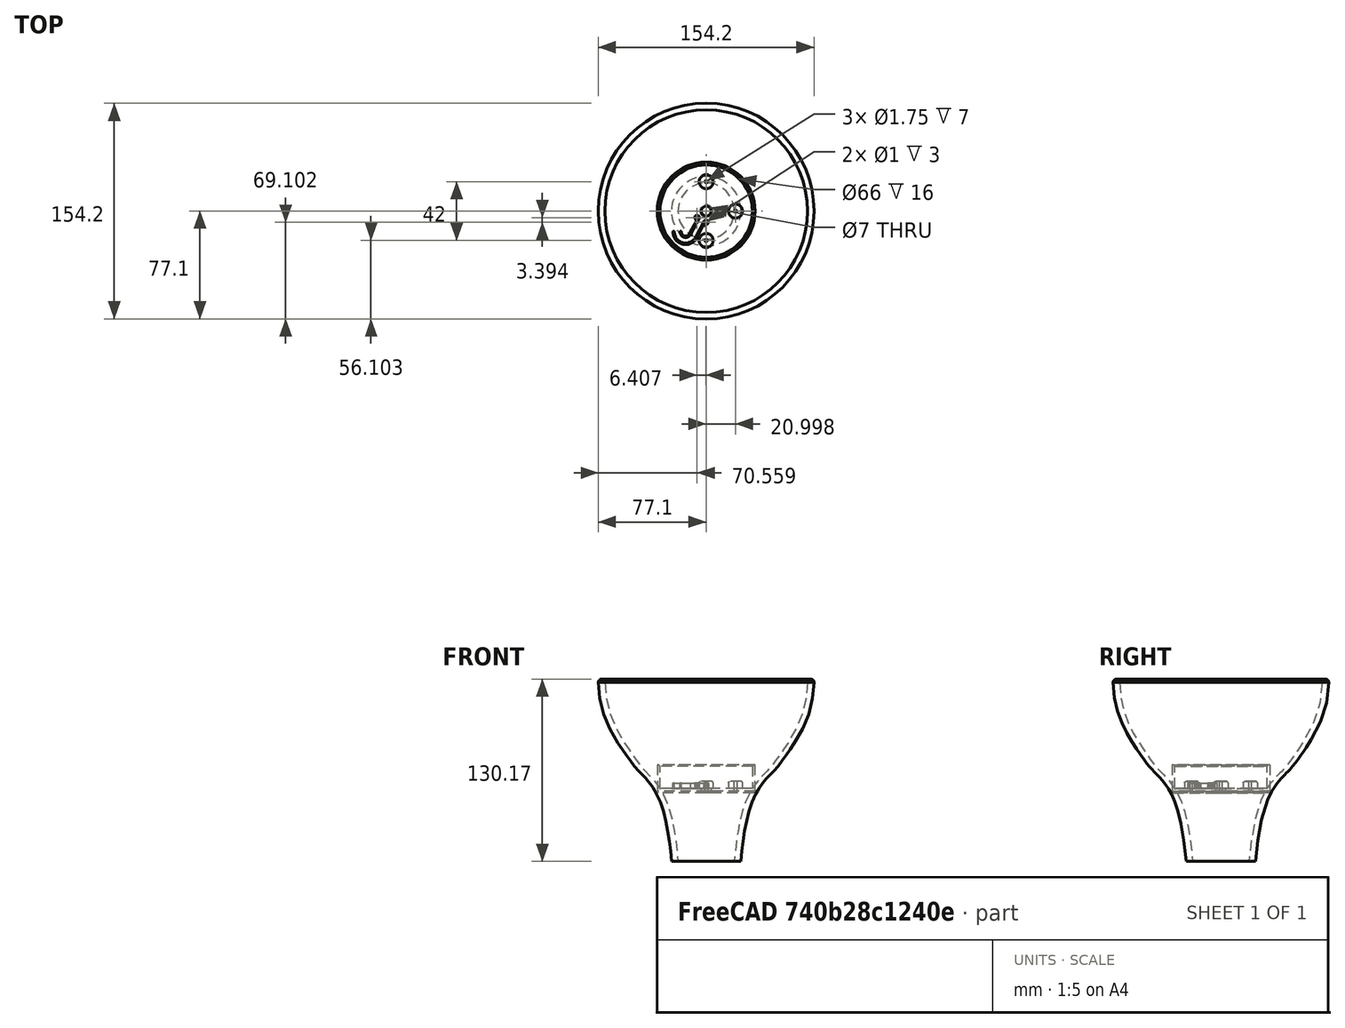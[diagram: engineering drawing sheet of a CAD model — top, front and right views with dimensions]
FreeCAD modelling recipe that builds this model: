
FCSTD DOCUMENT  (FreeCAD 0.21R33771 (Git))
Label: lampshade pre-merge
License: All rights reserved
LicenseURL: http://en.wikipedia.org/wiki/All_rights_reserved
objects: Sketcher::SketchObject×9, PartDesign::Pocket×4, PartDesign::Fillet×4, PartDesign::Pad×3, Part::Feature×2, PartDesign::Body×2, PartDesign::Chamfer×1, Mesh::Feature×1, Part::Refine×1, PartDesign::Revolution×1, App::Part×1
note: 40 computed .brp shape members not serialized (recipe doc carries the construction recipe); baked Part::Feature solids carry a one-line shape summary decoded from their .brp

FEATURE [Sketcher::SketchObject] Sketch001
  FullyConstrained = true
  MapMode = 5
  Support = -> [XY_Plane]
  sketch-geometry (1):
    g0: Circle CenterX=0 CenterY=0 CenterZ=0 NormalX=0 NormalY=0 NormalZ=1 AngleXU=0 Radius=35
  constraints (2):
    c: Coincident(g0,g-1)
    c: Diameter(g0) = 70
FEATURE [PartDesign::Pad] Pad
  Direction = (0,0,1)
  Length = 20
  Length2 = 10
  Profile = -> Sketch001
  ReferenceAxis = -> Sketch001 [N_Axis]
  Type = 0
FEATURE [Sketcher::SketchObject] Sketch
  FullyConstrained = true
  MapMode = 5
  Placement = pos=(0,0,20) rot=(0,0,1;0rad)
  Support = -> [Pad]
  sketch-geometry (1):
    g0: Circle CenterX=0 CenterY=0 CenterZ=0 NormalX=0 NormalY=0 NormalZ=1 AngleXU=0 Radius=33
  constraints (2):
    c: Coincident(g0,g-1)
    c: Diameter(g0) = 66
FEATURE [PartDesign::Pocket] Pocket
  BaseFeature = -> Pad
  Direction = (0,0,-1)
  Length = 17
  Length2 = 5
  Profile = -> Sketch
  ReferenceAxis = -> Sketch [N_Axis]
  Type = 0
FEATURE [Sketcher::SketchObject] Sketch002
  FullyConstrained = false
  MapMode = 5
  Placement = pos=(0,0,3) rot=(0,0,1;0rad)
  Support = -> [Pocket]
  sketch-geometry (4):
    g0: Circle CenterX=-0.00194019 CenterY=0.00345167 CenterZ=0 NormalX=0 NormalY=0 NormalZ=1 AngleXU=0 Radius=21
    g1: Circle CenterX=0 CenterY=21.0035 CenterZ=0 NormalX=0 NormalY=0 NormalZ=1 AngleXU=0 Radius=5
    g2: Circle CenterX=20.9981 CenterY=0 CenterZ=0 NormalX=0 NormalY=0 NormalZ=1 AngleXU=0 Radius=5
    g3: Circle CenterX=0 CenterY=-20.9965 CenterZ=0 NormalX=0 NormalY=0 NormalZ=1 AngleXU=0 Radius=5
  constraints (10):
    c: Diameter(g0) = 42
    c: PointOnObject(g1,g0)
    c: PointOnObject(g2,g0)
    c: PointOnObject(g3,g0)
    c: PointOnObject(g3,g-2)
    c: PointOnObject(g2,g-1)
    c: PointOnObject(g1,g-2)
    c: Equal(g1,g2)
    c: Equal(g2,g3)
    c: Diameter(g1) = 10
FEATURE [PartDesign::Pad] Pad001
  BaseFeature = -> Pocket
  Direction = (0,0,1)
  Length = 5
  Length2 = 10
  Profile = -> Sketch002
  ReferenceAxis = -> Sketch002 [N_Axis]
  Type = 0
FEATURE [Sketcher::SketchObject] Sketch003
  ExternalGeometry = -> [Pad001]
  FullyConstrained = true
  MapMode = 5
  Placement = pos=(0,0,8) rot=(0,0,1;0rad)
  Support = -> [Pad001]
  sketch-geometry (3):
    g0: Circle CenterX=0 CenterY=21.0035 CenterZ=0 NormalX=0 NormalY=0 NormalZ=1 AngleXU=0 Radius=0.875
    g1: Circle CenterX=0 CenterY=-20.9965 CenterZ=0 NormalX=0 NormalY=0 NormalZ=1 AngleXU=0 Radius=0.875
    g2: Circle CenterX=20.9981 CenterY=0 CenterZ=0 NormalX=0 NormalY=0 NormalZ=1 AngleXU=0 Radius=0.875
  constraints (6):
    c: Coincident(g0,g-3)
    c: Coincident(g1,g-4)
    c: Coincident(g2,g-5)
    c: Equal(g0,g1)
    c: Equal(g1,g2)
    c: Diameter(g0) = 1.75
FEATURE [PartDesign::Pocket] Pocket001
  BaseFeature = -> Pad001
  Direction = (0,0,-1)
  Length = 7
  Length2 = 5
  Profile = -> Sketch003
  ReferenceAxis = -> Sketch003 [N_Axis]
  Type = 0
FEATURE [Sketcher::SketchObject] Sketch004
  FullyConstrained = true
  MapMode = 5
  Placement = pos=(0,0,3) rot=(0,0,1;0rad)
  Support = -> [Pocket001]
  sketch-geometry (1):
    g0: Circle CenterX=0 CenterY=0 CenterZ=0 NormalX=0 NormalY=0 NormalZ=1 AngleXU=0 Radius=3.5
  constraints (3):
    c: PointOnObject(g0,g-1)
    c: Diameter(g0) = 7
    c: PointOnObject(g0,g-2)
FEATURE [PartDesign::Pocket] Pocket002
  BaseFeature = -> Pocket001
  Direction = (0,0,-1)
  Length = 10
  Length2 = 5
  Profile = -> Sketch004
  ReferenceAxis = -> Sketch004 [N_Axis]
  Type = 0
FEATURE [PartDesign::Chamfer] Chamfer
  Angle = 45
  Base = -> Pocket002 [Edge2,Edge5,Edge4]
  BaseFeature = -> Pocket002
  ChamferType = 0
  FlipDirection = false
  Size = 1
  Size2 = 1
  SupportTransform = false
  UseAllEdges = false
FEATURE [Sketcher::SketchObject] Sketch005
  ExternalGeometry = -> [Chamfer]
  FullyConstrained = false
  MapMode = 5
  Placement = pos=(0,0,3) rot=(0,0,1;0rad)
  Support = -> [Chamfer]
  sketch-geometry (21):
    g0: LineSegment StartX=0 StartY=0 StartZ=0 EndX=-12.3375 EndY=-23.2904 EndZ=0
    g1: LineSegment StartX=-3.33785 StartY=-6.30109 StartZ=0 EndX=-5.10519 EndY=-5.36488 EndZ=0
    g2: LineSegment StartX=-3.33785 StartY=-6.30109 StartZ=0 EndX=-1.5705 EndY=-7.2373 EndZ=0
    g3: ArcOfCircle CenterX=-0.134531 CenterY=-7.99797 CenterZ=0 NormalX=0 NormalY=0 NormalZ=1 AngleXU=0 Radius=1.625 StartAngle=3.81788 EndAngle=8.93763
    g4: ArcOfCircle CenterX=-6.54116 CenterY=-4.60421 CenterZ=0 NormalX=0 NormalY=0 NormalZ=1 AngleXU=0 Radius=1.625 StartAngle=5.79576 EndAngle=10.9054
    g5: ArcOfCircle CenterX=-14.6925 CenterY=-14.9185 CenterZ=0 NormalX=0 NormalY=0 NormalZ=1 AngleXU=0 Radius=4 StartAngle=3.14159 EndAngle=5.83833
    g6: LineSegment StartX=-11.1578 StartY=-16.7909 StartZ=0 EndX=-9.3905 EndY=-17.7271 EndZ=0
    g7: LineSegment StartX=-9.3905 StartY=-17.7271 StartZ=0 EndX=-7.62315 EndY=-18.6633 EndZ=0
    g8: LineSegment StartX=-14.9937 StartY=-18.9071 StartZ=0 EndX=-14.9184 EndY=-17.91 EndZ=0
    g9: ArcOfCircle CenterX=-14.6925 CenterY=-14.9185 CenterZ=0 NormalX=0 NormalY=0 NormalZ=1 AngleXU=0 Radius=3 StartAngle=3.14159 EndAngle=5.79576
    g10: LineSegment StartX=-8.32768 StartY=-19.765 StartZ=0 EndX=-7.53208 EndY=-20.3708 EndZ=0
    g11: LineSegment StartX=-11.0819 StartY=-16.6398 StartZ=0 EndX=-5.10541 EndY=-5.36528 EndZ=0
    g12: LineSegment StartX=-7.62315 StartY=-18.6633 StartZ=0 EndX=-1.5705 EndY=-7.2373 EndZ=0
    g13: LineSegment StartX=-6.48386 StartY=-18.6087 StartZ=0 EndX=-1.40187 EndY=-9.01506 EndZ=0
    g14: LineSegment StartX=-12.0419 StartY=-16.3235 StartZ=0 EndX=-6.68757 EndY=-6.2226 EndZ=0
    g15: LineSegment StartX=-14.6925 StartY=-14.9185 StartZ=0 EndX=-23.6925 EndY=-14.9185 EndZ=0
    g16: ArcOfCircle CenterX=-23.1925 CenterY=-14.9185 CenterZ=0 NormalX=0 NormalY=0 NormalZ=1 AngleXU=0 Radius=0.5 StartAngle=0 EndAngle=3.14159
    g17: ArcOfCircle CenterX=-18.1925 CenterY=-14.9185 CenterZ=0 NormalX=0 NormalY=0 NormalZ=1 AngleXU=0 Radius=0.5 StartAngle=-9e-16 EndAngle=3.14159
    g18: GeomPoint X=-22.6925 Y=-14.9185 Z=0
    g19: ArcOfCircle CenterX=-14.6925 CenterY=-14.9185 CenterZ=0 NormalX=0 NormalY=0 NormalZ=1 AngleXU=0 Radius=9 StartAngle=3.14159 EndAngle=5.86071
    g20: ArcOfCircle CenterX=-14.6925 CenterY=-14.9185 CenterZ=0 NormalX=0 NormalY=0 NormalZ=1 AngleXU=0 Radius=8 StartAngle=3.14159 EndAngle=5.79604
  constraints (45):
    c: Coincident(g0,g-3)
    c: Coincident(g2,g1)
    c: PointOnObject(g1,g0)
    c: Perpendicular(g0,g1)
    c: Perpendicular(g0,g2)
    c: Equal(g1,g2)
    c: Distance(g1,g2) = 4
    c: PointOnObject(g1,g4)
    c: Perpendicular(g4,g1)
    c: Equal(g4,g3)
    c: Diameter(g3) = 3.25
    c: Diameter(g5) = 8
    c: PointOnObject(g6,g5)
    c: Coincident(g7,g6)
    c: Perpendicular(g5,g6)
    c: Equal(g6,g7)
    c: PointOnObject(g6,g0)
    c: Perpendicular(g0,g6)
    c: PointOnObject(g8,g5)
    c: Perpendicular(g5,g8)
    c: Distance(g8) = 1  'cable guide wall thickness'
    c: Coincident(g9,g5)
    c: PointOnObject(g8,g9)
    c: Equal(g8,g10)
    c: Tangent(g12,g3) = 1.5708
    c: Parallel(g14,g11)
    c: Parallel(g12,g13)
    c: Coincident(g15,g5)
    c: Horizontal(g15)
    c: PointOnObject(g16,g15)
    c: PointOnObject(g17,g15)
    c: PointOnObject(g18,g16)
    c: Coincident(g19,g13)
    c: Coincident(g20,g12) = -1.5708
    c: Perpendicular(g3,g2) = 1.5708
    c: Coincident(g3,g13)
    c: Coincident(g4,g14)
    c: Tangent(g4,g11) = -1.5708
    c: Tangent(g16,g19) = -1.5708
    c: Tangent(g16,g20) = 1.5708
    c: Tangent(g17,g9) = 1.5708
    c: Tangent(g5,g17) = -1.5708
    c: Tangent(g9,g14) = -1.5708
    c: PointOnObject(g9,g15)
    c: Coincident(g5,g11)
FEATURE [PartDesign::Pad] Pad002
  BaseFeature = -> Chamfer
  Direction = (0,0,1)
  Length = 3.75
  Length2 = 10
  Profile = -> Sketch005
  ReferenceAxis = -> Sketch005 [N_Axis]
  Type = 0
FEATURE [Sketcher::SketchObject] Sketch006
  ExternalGeometry = -> [Pad002]
  FullyConstrained = true
  MapMode = 5
  Placement = pos=(0,0,6.75) rot=(0,0,1;0rad)
  Support = -> [Pad002]
  sketch-geometry (2):
    g0: Circle CenterX=-6.54116 CenterY=-4.60421 CenterZ=0 NormalX=0 NormalY=0 NormalZ=1 AngleXU=0 Radius=0.5
    g1: Circle CenterX=-0.134531 CenterY=-7.99797 CenterZ=0 NormalX=0 NormalY=0 NormalZ=1 AngleXU=0 Radius=0.5
  constraints (4):
    c: Coincident(g0,g-3)
    c: Coincident(g1,g-4)
    c: Equal(g0,g1)
    c: Diameter(g0) = 1
FEATURE [PartDesign::Pocket] Pocket003
  BaseFeature = -> Pad002
  Direction = (0,0,-1)
  Length = 3
  Length2 = 5
  Profile = -> Sketch006
  ReferenceAxis = -> Sketch006 [N_Axis]
  Type = 0
FEATURE [PartDesign::Fillet] Fillet
  Base = -> Pocket003 [Edge15]
  BaseFeature = -> Pocket003
  Radius = 1
  SupportTransform = false
  UseAllEdges = false
FEATURE [PartDesign::Fillet] Fillet001
  Base = -> Fillet [Edge21]
  BaseFeature = -> Fillet
  Radius = 1
  SupportTransform = false
  UseAllEdges = false
FEATURE [PartDesign::Fillet] Fillet002
  Base = -> Fillet001 [Edge13]
  BaseFeature = -> Fillet001
  Radius = 1
  SupportTransform = false
  UseAllEdges = false
FEATURE [PartDesign::Fillet] Fillet003
  Base = -> Fillet002 [Edge49,Edge47,Edge51]
  BaseFeature = -> Fillet002
  Radius = 1
  SupportTransform = false
  UseAllEdges = false
FEATURE [Mesh::Feature] Head_v1
FEATURE [Part::Feature] Head_v002
  shape: large baked B-rep (101 MB .brp); summary skipped
FEATURE [Part::Refine] Head_v003
  Source = -> Head_v002
FEATURE [Part::Feature] Head_v003_cs
  shape: bbox 3e-07 x 154.9 x 129.2 mm, 0 faces, 0 solids (baked)
FEATURE [Sketcher::SketchObject] Sketch007
  FullyConstrained = false
  Placement = pos=(0,0,0) rot=(0,1,0;1.5708rad)
  sketch-geometry (18):
    g0: GeomPoint X=-127.837 Y=-77.1037 Z=0
    g1: BSplineCurve PolesCount=7 KnotsCount=5 Degree=3 IsPeriodic=0
    g2-g8: Circle x7 (B-spline internal-alignment scaffolding for g1; pole/knot coordinates omitted)
    g9-g13: GeomPoint x5 (B-spline internal-alignment scaffolding for g1; pole/knot coordinates omitted)
    g14: LineSegment StartX=-127.837 StartY=-77.1037 StartZ=0 EndX=-127.837 EndY=-72.4339 EndZ=0
    g15: BSplineCurve PolesCount=7 KnotsCount=5 Degree=3 IsPeriodic=0
    g16: LineSegment StartX=0 StartY=-24.806 StartZ=0 EndX=0 EndY=-20.1362 EndZ=0
    g17: ArcOfCircle CenterX=-127.837 CenterY=-74.7688 CenterZ=0 NormalX=0 NormalY=0 NormalZ=1 AngleXU=0 Radius=2.33488 StartAngle=1.5708 EndAngle=4.71239
  constraints (26):
    c: Block(g1)
    c: InternalAlignment(g2,g1)
    c: Weight(g2) = 1
    c: InternalAlignment(g3,g1)
    c: Equal(g3,g2)
    c: InternalAlignment(g4,g1)
    c: Equal(g4,g2)
    c: InternalAlignment(g5,g1)
    c: Equal(g5,g2)
    c: InternalAlignment(g6,g1)
    c: Equal(g6,g2)
    c: InternalAlignment(g7,g1)
    c: Equal(g7,g2)
    c: InternalAlignment(g8,g1)
    c: Equal(g8,g2)
    c: InternalAlignment(g9-g13 -> g1) x5
    c: Coincident(g14,g1)
    c: Vertical(g14)
    c: Block(g15)
    c: Coincident(g16,g1)
    c: Coincident(g16,g15)
    c: Vertical(g16)
    c: PointOnObject(g15,g17)
    c: PointOnObject(g17,g14)
    c: Coincident(g17,g14)
    c: Coincident(g17,g1)
FEATURE [PartDesign::Revolution] Revolution
  Angle = 360
  Axis = (2e-16,0,-1)
  Base = (0,0,0)
  Placement = pos=(0,0,0) rot=(0,1,0;1.5708rad)
  Profile = -> Sketch007
  ReferenceAxis = -> Sketch007 [H_Axis]
  Reversed = true
FEATURE [PartDesign::Body] Body001  label="Lampshade"
  Group = -> [Sketch007,Revolution]
  Origin = -> Origin002
  Tip = -> Revolution
FEATURE [Sketcher::SketchObject] Sketch008
  FullyConstrained = true
  MapMode = 5
  Placement = pos=(0,0,20) rot=(0,0,1;0rad)
  Support = -> [Fillet003]
FEATURE [PartDesign::Body] Body  label="Webcam Mount"
  Group = -> [Sketch,Sketch001,Pad,Pocket,Sketch002,Pad001,Sketch003,Pocket001,Sketch004,Pocket002,Chamfer,Sketch005,Pad002,Sketch006,Pocket003,Fillet,Fillet001,Fillet002,Fillet003,Sketch008]
  Origin = -> Origin
  Placement = pos=(0,0,49) rot=(0,0,1;0rad)
  Tip = -> Fillet003
FEATURE [App::Part] Part
  Group = -> [Body,Body001]
  Origin = -> Origin001
